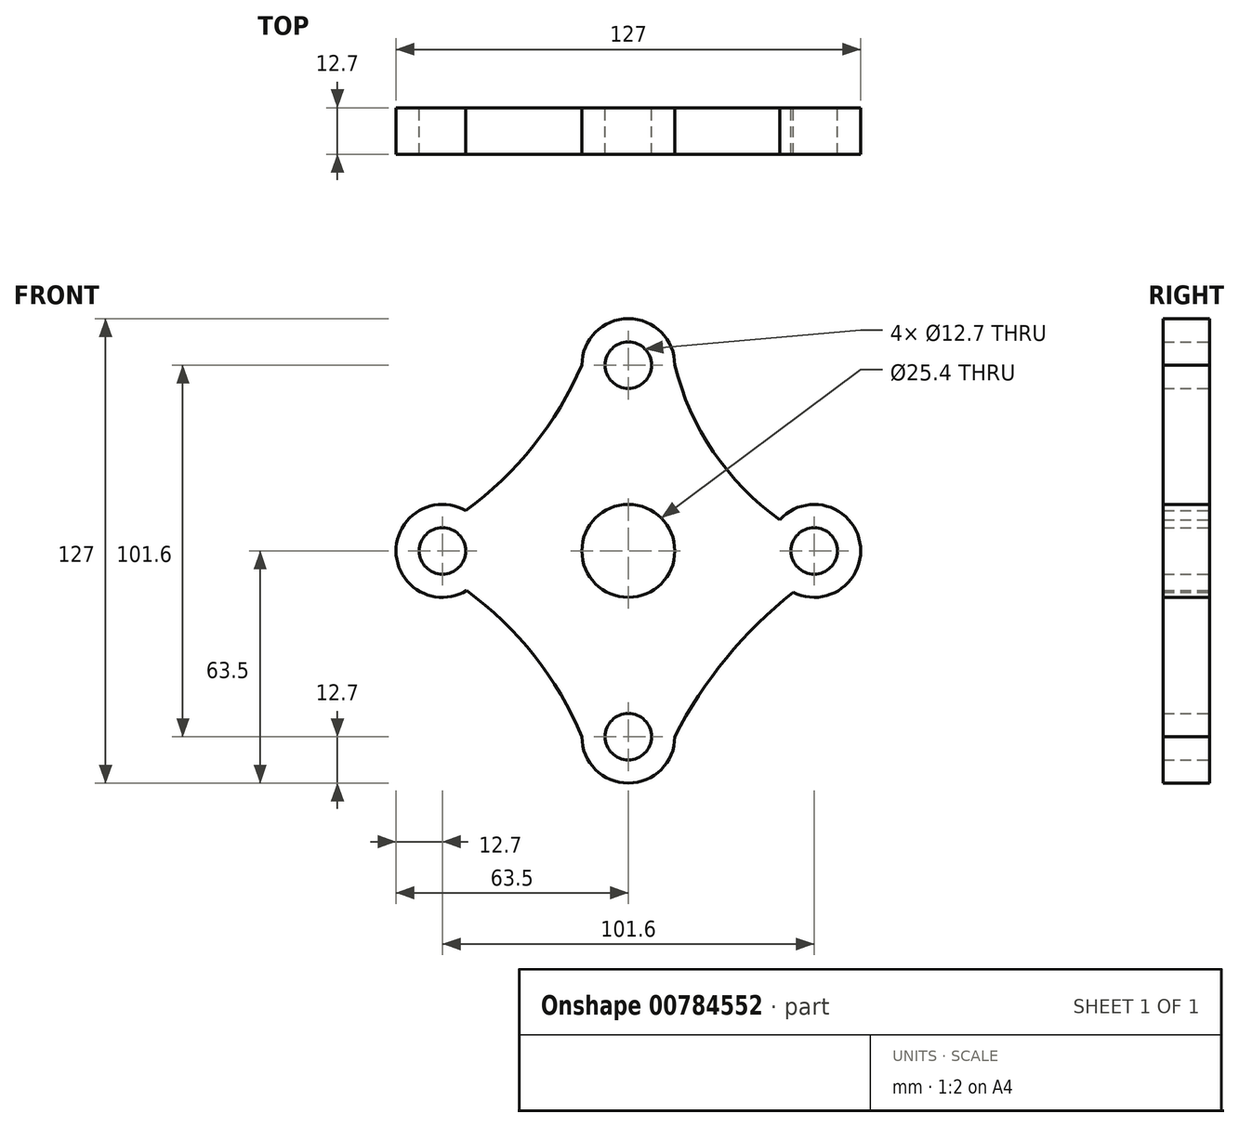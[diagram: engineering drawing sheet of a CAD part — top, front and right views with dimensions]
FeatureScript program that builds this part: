
annotation { "Feature Type Name" : "Feature", "Feature Type Description" : "" }
export const myFeature = defineFeature(function(context is Context, id is Id, definition is map)
    precondition{}
    {
        {
            var Q0;
            Q0=qCreatedBy(makeId("Front.planeOp"),FACE);
            var sketch = newSketch(context, id + "F0", { "sketchPlane" : qUnion([Q0])});
            skCircle(sketch, "E0", {"center": v(0, 0) * mm, "radius": 12.7 * mm});
            skCircle(sketch, "E1", {"center": v(0, 50.8) * mm, "radius": 6.35 * mm});
            skCircle(sketch, "E2", {"center": v(0, -50.8) * mm, "radius": 6.35 * mm});
            skCircle(sketch, "E3", {"center": v(50.8, 0) * mm, "radius": 6.35 * mm});
            skCircle(sketch, "E4", {"center": v(-50.8, 0) * mm, "radius": 6.35 * mm});
            skCircle(sketch, "E5", {"center": v(-50.8, 0) * mm, "radius": 12.7 * mm});
            skCircle(sketch, "E6", {"center": v(0, 50.8) * mm, "radius": 12.7 * mm});
            skCircle(sketch, "E7", {"center": v(50.8, 0) * mm, "radius": 12.7 * mm});
            skCircle(sketch, "E8", {"center": v(0, -50.8) * mm, "radius": 12.7 * mm});
            skArc(sketch, "E9", {"start": v(-63.5, 0) * mm, "mid": v(-33.27, 20.57) * mm, "end": v(-12.7, 50.8) * mm});
            skArc(sketch, "E10", {"start": v(-12.7, -50.8) * mm, "mid": v(-33.08, -20.38) * mm, "end": v(-63.5, 0) * mm});
            skArc(sketch, "E11", {"start": v(56.08, -3.53) * mm, "mid": v(31.17, -24.2) * mm, "end": v(12.7, -50.8) * mm});
            skArc(sketch, "E12", {"start": v(12.7, 50.8) * mm, "mid": v(28.75, 20) * mm, "end": v(57.15, 0) * mm});
            skSolve(sketch);
        }
        {
            var Q0;
            Q0 = qSketchRegion(id + "F0", true);
            extrude(context, id + "F1", {"entities" : qUnion([Q0]), "depth" : 12.7 * mm, "offsetDistance" : 25.4 * mm});
        }
    });
